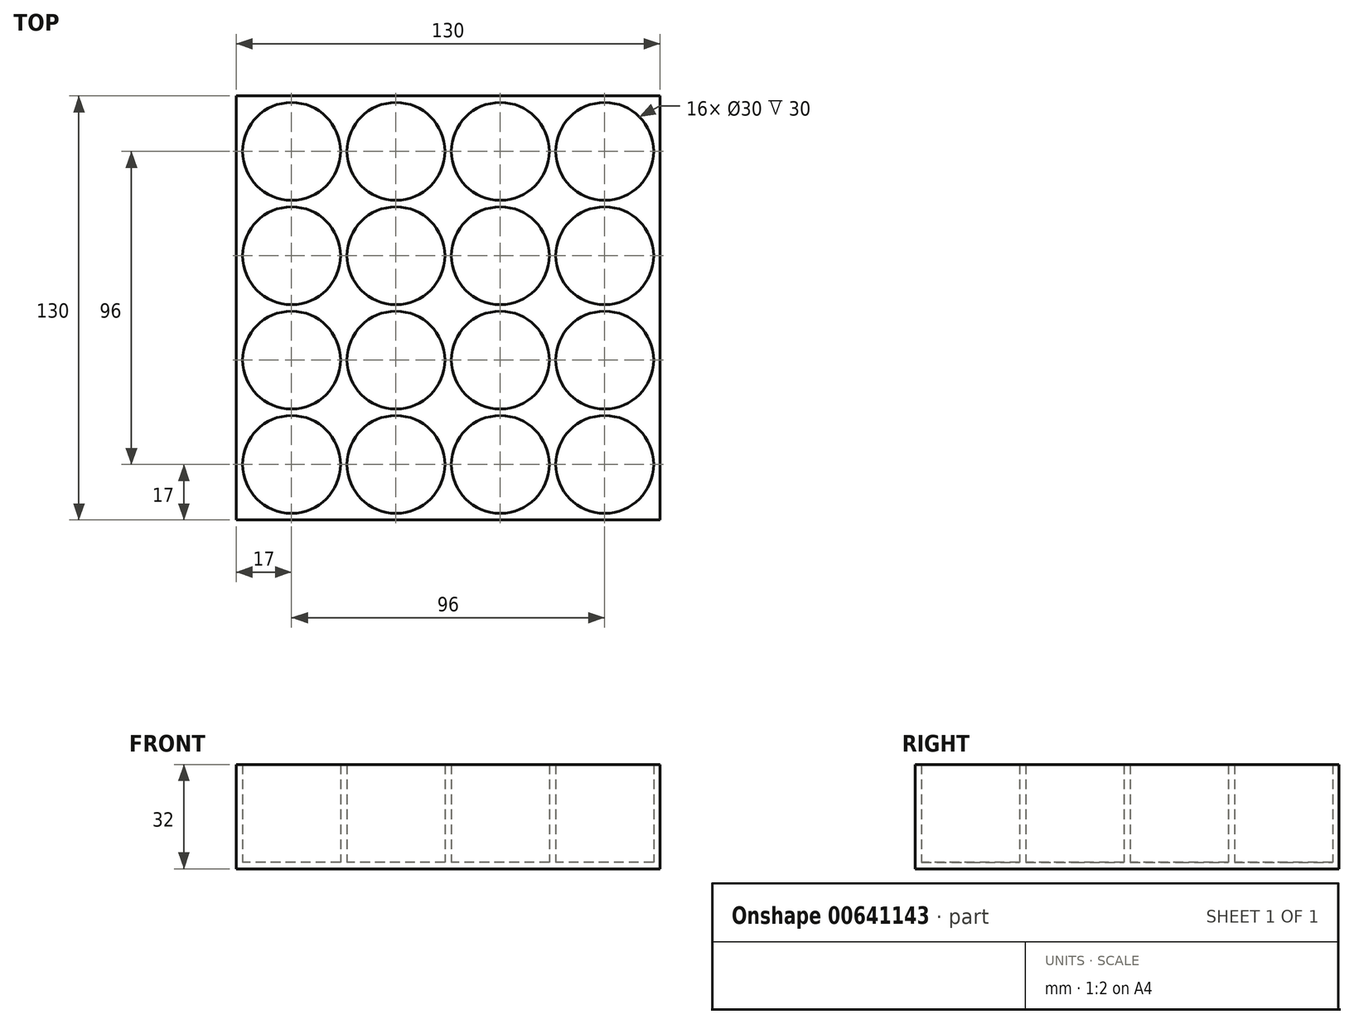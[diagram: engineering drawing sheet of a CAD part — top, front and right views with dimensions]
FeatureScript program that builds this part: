
annotation { "Feature Type Name" : "Feature", "Feature Type Description" : "" }
export const myFeature = defineFeature(function(context is Context, id is Id, definition is map)
    precondition{}
    {
        {
            var Q0;
            Q0=qCreatedBy(makeId("Top.planeOp"),FACE);
            var sketch = newSketch(context, id + "F0", { "sketchPlane" : qUnion([Q0])});
            skLineSegment(sketch, "E0.bottom", {"start": v(-75, 75) * mm, "end": v(55, 75) * mm});
            skLineSegment(sketch, "E0.top", {"start": v(-75, -55) * mm, "end": v(55, -55) * mm});
            skLineSegment(sketch, "E0.left", {"start": v(-75, 75) * mm, "end": v(-75, -55) * mm});
            skLineSegment(sketch, "E0.right", {"start": v(55, 75) * mm, "end": v(55, -55) * mm});
            skSolve(sketch);
        }
        {
            var Q0;
            Q0 = qSketchRegion(id + "F0", true);
            extrude(context, id + "F1", {"entities" : qUnion([Q0]), "depth" : 2 * mm, "offsetDistance" : 25 * mm});
        }
        {
            var Q0;
            Q0=makeQuery(id+"F1.opExtrude","CAP_FACE",FACE,{"disambiguationData":[OSD([sQuery(id+"F0.wireOp",EDGE,"E0.bottom"),sQuery(id+"F0.wireOp",EDGE,"E0.top"),sQuery(id+"F0.wireOp",EDGE,"E0.left"),sQuery(id+"F0.wireOp",EDGE,"E0.right")])],"isStart":false});
            var sketch = newSketch(context, id + "F2", { "sketchPlane" : qUnion([Q0])});
            skCircle(sketch, "E1", {"center": v(-58, 58) * mm, "radius": 15 * mm});
            skLineSegment(sketch, "E2", {"start": v(-58, 75) * mm, "end": v(-58, -55) * mm, "construction": true});
            skCircle(sketch, "E3", {"center": v(-58, 26) * mm, "radius": 15 * mm});
            skCircle(sketch, "E4", {"center": v(-58, -6) * mm, "radius": 15 * mm});
            skCircle(sketch, "E5", {"center": v(-58, -38) * mm, "radius": 15 * mm});
            skLineSegment(sketch, "E6", {"start": v(-42, 75) * mm, "end": v(-42, -55) * mm, "construction": true});
            skCircle(sketch, "E7.MirrorC", {"center": v(-26, 58) * mm, "radius": 15 * mm});
            skCircle(sketch, "E8.MirrorC", {"center": v(-26, 26) * mm, "radius": 15 * mm});
            skCircle(sketch, "E9.MirrorC", {"center": v(-26, -6) * mm, "radius": 15 * mm});
            skCircle(sketch, "E10.MirrorC", {"center": v(-26, -38) * mm, "radius": 15 * mm});
            skLineSegment(sketch, "E11", {"start": v(-10, 75) * mm, "end": v(-10, -55) * mm, "construction": true});
            skCircle(sketch, "E12.MirrorC", {"center": v(38, -38) * mm, "radius": 15 * mm});
            skCircle(sketch, "E13.MirrorC", {"center": v(38, -6) * mm, "radius": 15 * mm});
            skCircle(sketch, "E14.MirrorC", {"center": v(38, 26) * mm, "radius": 15 * mm});
            skCircle(sketch, "E15.MirrorC", {"center": v(38, 58) * mm, "radius": 15 * mm});
            skCircle(sketch, "E16.MirrorC", {"center": v(6, 58) * mm, "radius": 15 * mm});
            skCircle(sketch, "E17.MirrorC", {"center": v(6, 26) * mm, "radius": 15 * mm});
            skCircle(sketch, "E18.MirrorC", {"center": v(6, -6) * mm, "radius": 15 * mm});
            skCircle(sketch, "E19.MirrorC", {"center": v(6, -38) * mm, "radius": 15 * mm});
            skLineSegment(sketch, "E20.bottom", {"start": v(-75, 75) * mm, "end": v(55, 75) * mm});
            skLineSegment(sketch, "E20.top", {"start": v(-75, -55) * mm, "end": v(55, -55) * mm});
            skLineSegment(sketch, "E20.left", {"start": v(-75, 75) * mm, "end": v(-75, -55) * mm});
            skLineSegment(sketch, "E20.right", {"start": v(55, 75) * mm, "end": v(55, -55) * mm});
            skSolve(sketch);
        }
        {
            var Q0;
            Q0 = qSketchRegion(id + "F2", true);
            extrude(context, id + "F3", {"entities" : qUnion([Q0]), "operationType" : NewBodyOperationType.ADD, "depth" : 30 * mm, "offsetDistance" : 25 * mm});
        }
    });
